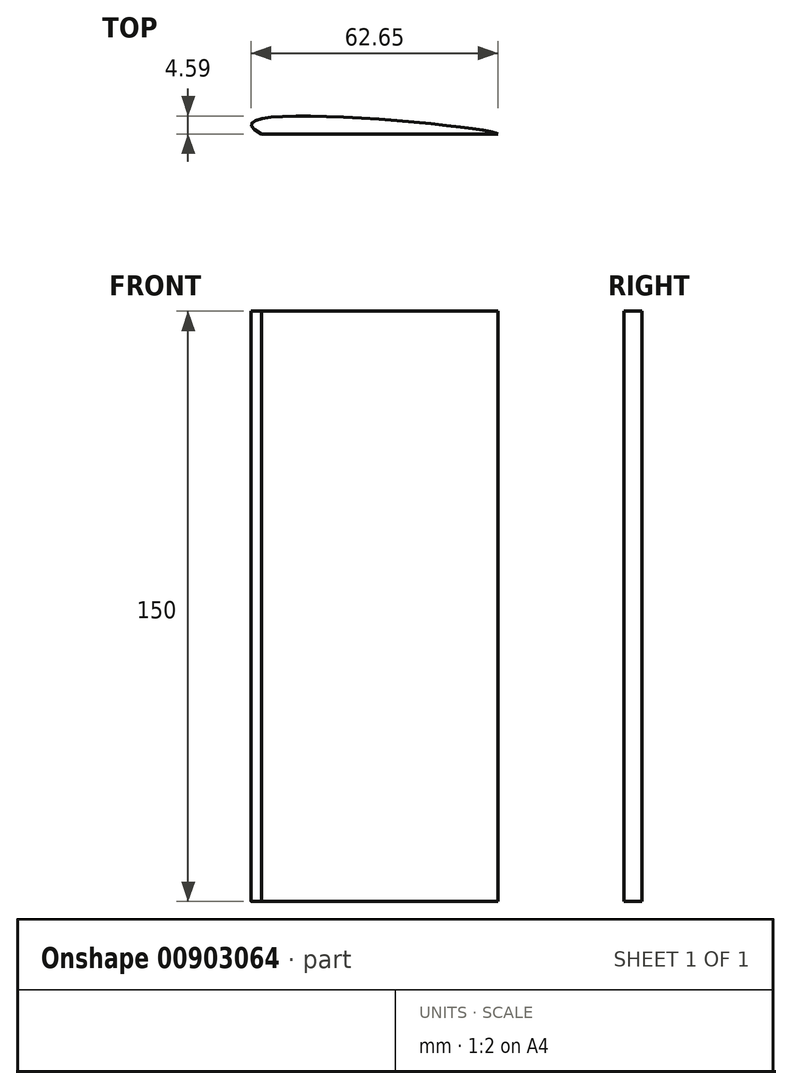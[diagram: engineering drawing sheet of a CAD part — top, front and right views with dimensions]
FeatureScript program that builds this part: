
annotation { "Feature Type Name" : "Feature", "Feature Type Description" : "" }
export const myFeature = defineFeature(function(context is Context, id is Id, definition is map)
    precondition{}
    {
        {
            var Q0;
            Q0=qCreatedBy(makeId("Top.planeOp"),FACE);
            var sketch = newSketch(context, id + "F0", { "sketchPlane" : qUnion([Q0])});
            skLineSegment(sketch, "E0", {"start": v(-31.42, 9.06) * mm, "end": v(28.58, 9.06) * mm});
            skFitSpline(sketch, "E1", {"points": [v(-31.42, 9.06) * mm, v(28.58, 9.06) * mm], "startDerivative": vector(-53.26, 27.96) * mm, "endDerivative": vector(2.05, -5.57) * mm});
            skSolve(sketch);
        }
        {
            var Q0;
            Q0 = qSketchRegion(id + "F0", true);
            extrude(context, id + "F1", {"entities" : qUnion([Q0]), "depth" : 150 * mm, "offsetDistance" : 25 * mm, "symmetric" : true});
        }
    });
